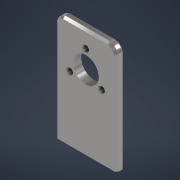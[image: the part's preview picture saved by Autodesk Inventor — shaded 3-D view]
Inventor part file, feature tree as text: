
AUTODESK INVENTOR PART (.ipt)
format: ipt  version: 2021 (Build 250183000, 183)  size: 138,752 bytes
history: native  units: mm
features: sketch x3, extrude x2, fillet x1, hole x1, chamfer x1
ambient origin geometry x8: Origin, YZ Plane, XZ Plane, XY Plane, X Axis, Y Axis, Z Axis, Center Point
bodies: Solid1 (feature_tree)
feature tree (8):
  extrude  "Extrusion1"  Depth=106.0mm
  fillet  "Fillet1"  Radius=30.0mm
  hole  "Hole1"  [1 undecoded]
  extrude  "Extrusion2"  TaperAngle=120.0deg  [1 undecoded]
  chamfer  "Chamfer1"  Angle=120.0deg  [1 undecoded]
  sketch  "Sketch1"  dims[d0=60.0mm d1=106.0mm d2=30.0mm]
  sketch  "Sketch2"  dims[d3=8.0mm d4=0.0mm d5=10.0mm]
  sketch  "Sketch3"  dims[d6=36.0mm d7=120.0deg d8=120.0deg d9=0.0mm d10=72.0mm d11=6.0mm d12=6.0mm d13=4.0mm d14=2.0mm d15=90.0deg d16=8.0mm d17=20.594885mm d18=72.0mm d19=0.0mm d20=25.0mm d21=0.0mm d22=0.0mm d23=2.0mm d24=2.0mm d25=45.0deg]
note: 3 required parameter values undecoded (feature->parameter linkage not recoverable at this tier; creation-order binding heuristic only, values carry confidence <= 0.55)
